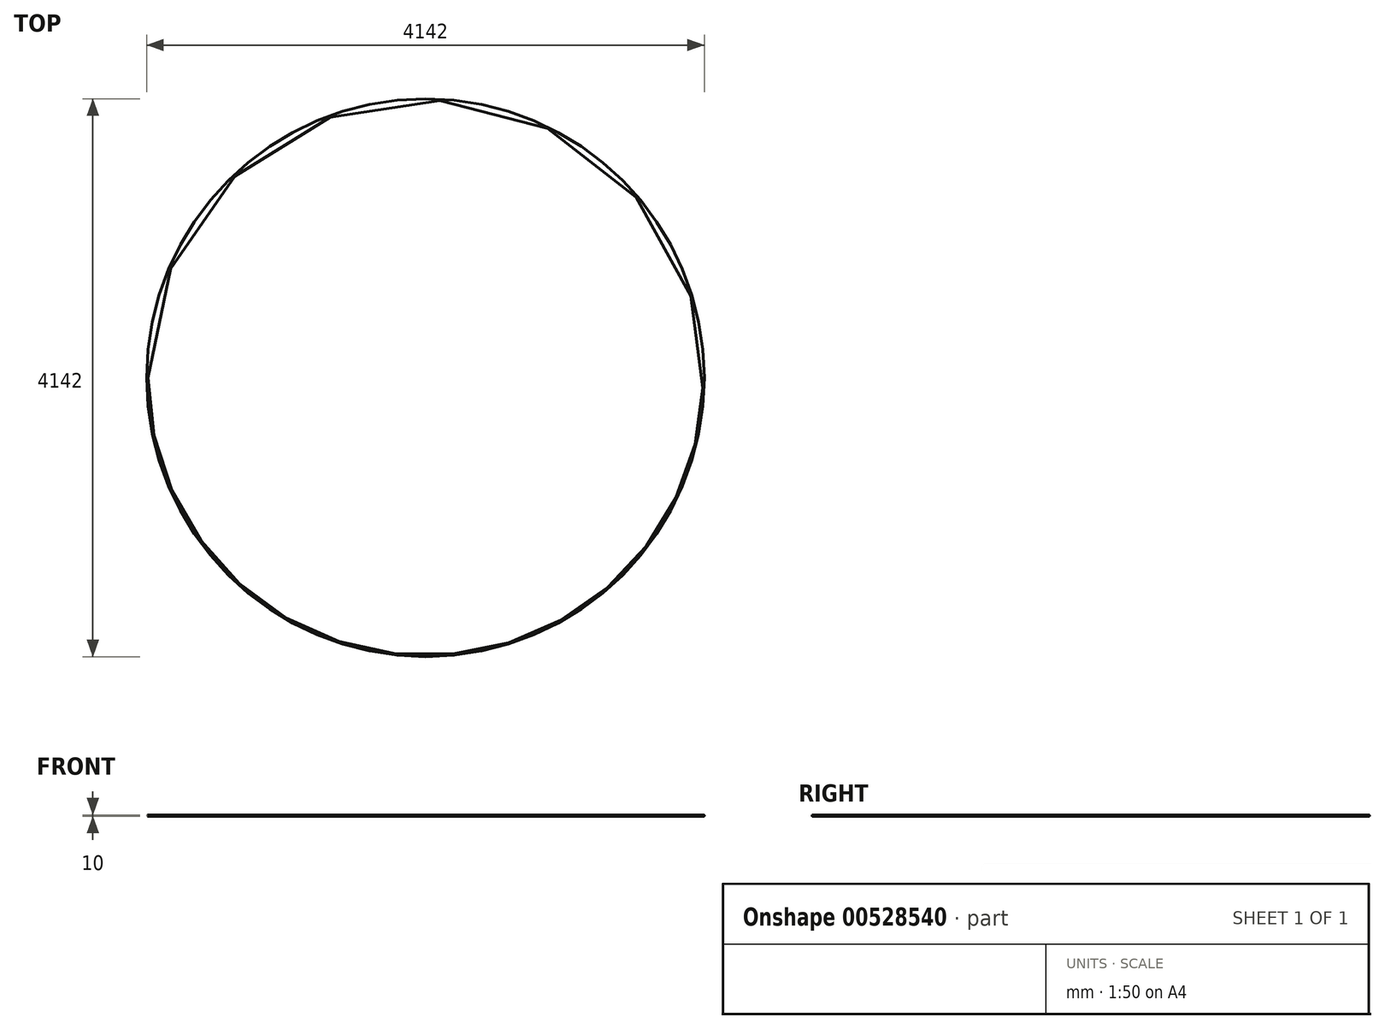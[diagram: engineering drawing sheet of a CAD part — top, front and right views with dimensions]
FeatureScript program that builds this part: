
annotation { "Feature Type Name" : "Feature", "Feature Type Description" : "" }
export const myFeature = defineFeature(function(context is Context, id is Id, definition is map)
    precondition{}
    {
        {
            var Q0;
            Q0=qCreatedBy(makeId("Right.planeOp"),FACE);
            var sketch = newSketch(context, id + "F0", { "sketchPlane" : qUnion([Q0])});
            skCircle(sketch, "E0", {"center": v(2066, 0) * mm, "radius": 5 * mm});
            skLineSegment(sketch, "E1", {"start": v(0, 0) * mm, "end": v(0, 513.48) * mm, "construction": true});
            skSolve(sketch);
        }
        {
            var Q0;
            Q0=qSketchRegion(id+"F0",true);
            var Q1;
            Q1=sQuery(id+"F0.wireOp",EDGE,"E1");
            revolve(context, id + "F1", {"entities" : qUnion([Q0]), "axis" : qUnion([Q1]), "revolveType" : RevolveType.FULL});
        }
    });
